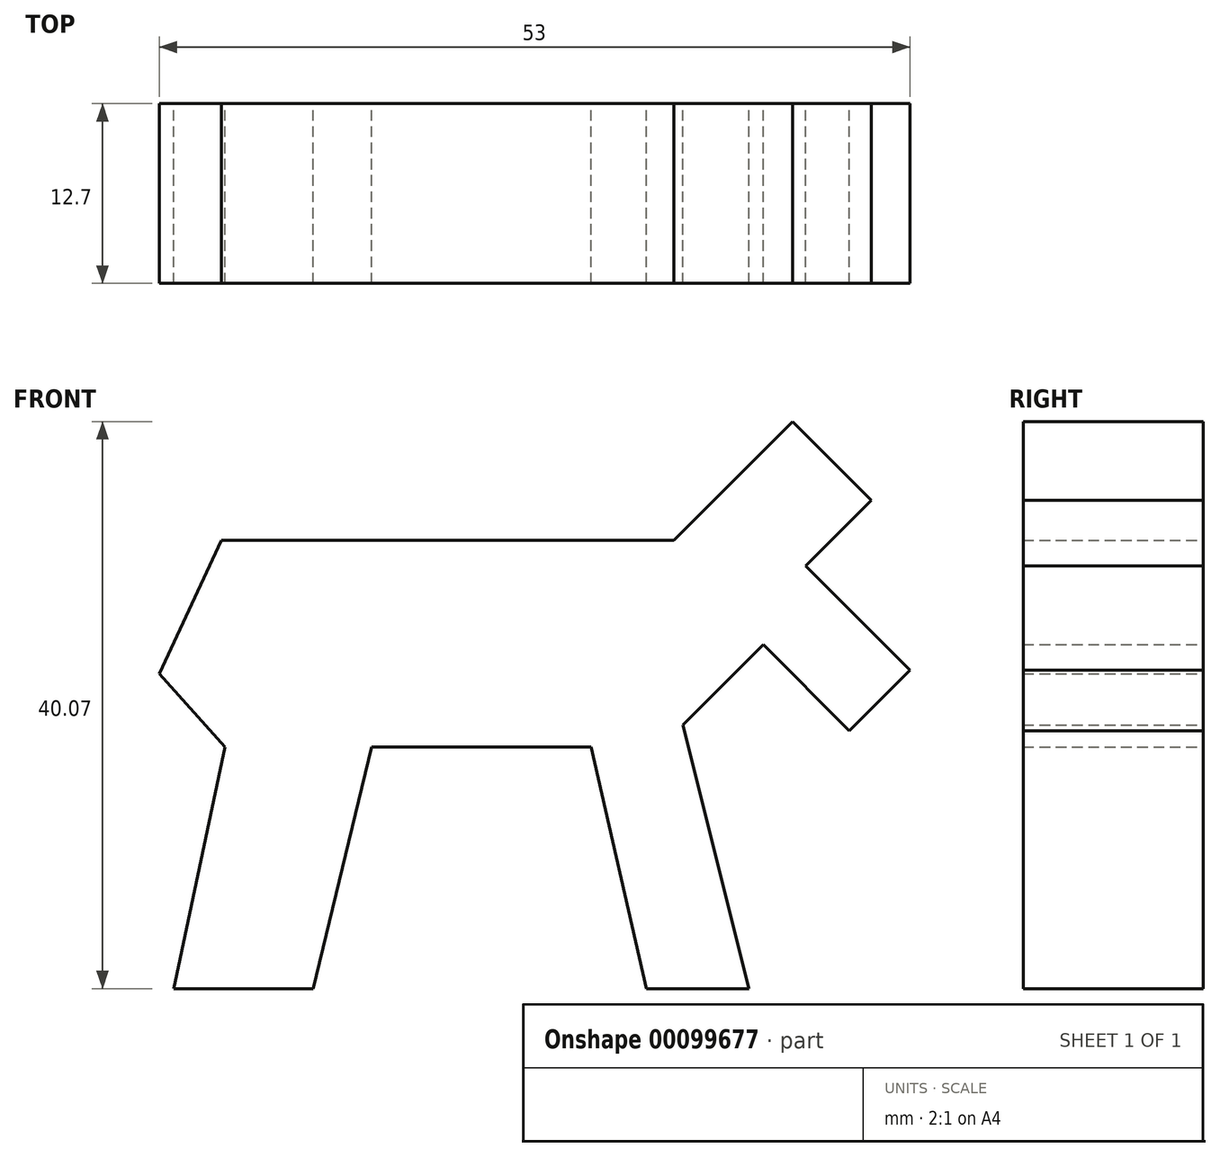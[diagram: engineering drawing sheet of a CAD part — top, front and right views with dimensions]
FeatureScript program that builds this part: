
annotation { "Feature Type Name" : "Feature", "Feature Type Description" : "" }
export const myFeature = defineFeature(function(context is Context, id is Id, definition is map)
    precondition{}
    {
        {
            var Q0;
            Q0=qCreatedBy(makeId("Front.planeOp"),FACE);
            var sketch = newSketch(context, id + "F0", { "sketchPlane" : qUnion([Q0])});
            skLineSegment(sketch, "E0", {"start": v(-47.7, -1.42) * mm, "end": v(-37.87, -1.42) * mm});
            skLineSegment(sketch, "E1", {"start": v(-37.87, -1.42) * mm, "end": v(-33.74, 15.64) * mm});
            skLineSegment(sketch, "E2", {"start": v(-33.74, 15.64) * mm, "end": v(-18.23, 15.64) * mm});
            skLineSegment(sketch, "E3", {"start": v(-18.23, 15.64) * mm, "end": v(-14.35, -1.42) * mm});
            skLineSegment(sketch, "E4", {"start": v(-14.35, -1.42) * mm, "end": v(-7.1, -1.42) * mm});
            skLineSegment(sketch, "E5", {"start": v(-7.1, -1.42) * mm, "end": v(-11.76, 17.2) * mm});
            skLineSegment(sketch, "E6", {"start": v(-11.76, 17.2) * mm, "end": v(-6.08, 22.88) * mm});
            skLineSegment(sketch, "E7", {"start": v(-6.08, 22.88) * mm, "end": v(0, 16.8) * mm});
            skLineSegment(sketch, "E8", {"start": v(0, 16.8) * mm, "end": v(4.27, 21.07) * mm});
            skLineSegment(sketch, "E9", {"start": v(4.27, 21.07) * mm, "end": v(-3.1, 28.44) * mm});
            skLineSegment(sketch, "E10", {"start": v(-3.1, 28.44) * mm, "end": v(1.55, 33.09) * mm});
            skLineSegment(sketch, "E11", {"start": v(1.55, 33.09) * mm, "end": v(-4, 38.65) * mm});
            skLineSegment(sketch, "E12", {"start": v(-4, 38.65) * mm, "end": v(-12.4, 30.25) * mm});
            skLineSegment(sketch, "E13", {"start": v(-12.4, 30.25) * mm, "end": v(-44.34, 30.25) * mm});
            skLineSegment(sketch, "E14", {"start": v(-44.34, 30.25) * mm, "end": v(-48.73, 20.81) * mm});
            skLineSegment(sketch, "E15", {"start": v(-48.73, 20.81) * mm, "end": v(-44.08, 15.64) * mm});
            skLineSegment(sketch, "E16", {"start": v(-44.08, 15.64) * mm, "end": v(-47.7, -1.42) * mm});
            skSolve(sketch);
        }
        {
            var Q0;
            Q0 = qSketchRegion(id + "F0", true);
            extrude(context, id + "F1", {"entities" : qUnion([Q0]), "depth" : 12.7 * mm});
        }
    });
